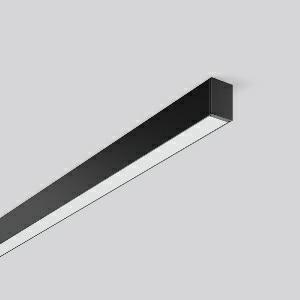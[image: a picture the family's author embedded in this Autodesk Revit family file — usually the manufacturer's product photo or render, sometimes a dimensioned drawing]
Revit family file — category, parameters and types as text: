
# Revit family: less_is_more_27_312200_003_76_f4a9
name_source: partatom
category: Lighting Fixtures
units: mm (PartAtom-declared; Revit-internal decimal feet)

## family parameters
Cut with Voids When Loaded = No
Host = Face
Light Source = No
Part Type = Normal
Room Calculation Point = No
Round Connector Dimension = Use Diameter
Shared = No

## types (1)
- LESS IS MORE 27 (1 x LED Modul 830, 2400 lm, 3000)
    Apparent Load = 43 VA
    CIE Flux Codes = 48 79 96 100 100
    Color Rendering = 80
    Color Temperature = 3000
    Default Elevation = 1800 mm
    Description = Series: LESS IS MORE 27
Ceiling and wall luminaire with slim design. Housing: extruded aluminium profile, powder-coated. End cap aluminium powder-coated. Diffuser made of non-yellowing plastic (PMMA), opal. Suitable for Ceiling mounting, Wall (surface). External driver with connecting cable. 
Colour: deep black, matt (RAL 9005)
Length: 1512 mm
Width: 28 mm
Height: 38 mm
Lamp: LED
Socket: without socket
Colour temperature: 3000K
Colour rendering index (CRI): 82
System power: 43 W
Rated luminous flux: 2400 lm
Luminous efficiency: 56 lm/W
Control gear: Voltage converter, DALI dim.
Protection class: II
Type of protection: IP 20
    Height = 38 mm
    Lamp = 1 x LED Modul 830
    Lamp Light Flux = 2400 lm
    Lamp count = 1
    Length = 1512 mm
    Lifetime = 50000 h
    Luminous efficacy = 56 lm/W
    Manufacturer = RZB
    ModVariant = No
    Model = 312200.003.76
    Mounting Place = Ceiling, Wall
    Mounting Type = Surface mounted
    Number of Poles = 1
    OnlyDefault = Yes
    Power Factor = 1
    Product Name = LESS IS MORE 27
    Product group = Surface mounted LED linear luminaires
    ProductGroupID = 307
    Protection Class = Protection class II
    Protection Degree = IP 20
    RLX_Detail_Level = 1
    RLX_Emergency_Light_Flux = 0 lm
    RLX_Emergency_Type = 0
    RLX_Emergency_Type_DB = No
    RlxData = <blob elided: 28741 chars, md5=8c4a918a>
    Socket = socket
    Standby Power = 0 W
    System Light Flux = 2400 lm
    System Power = 43 W
    Type Comments = Product without accessories
    Type Image = 312196.003.jpg
    URL = http://relux.com
    VarID = ---
    Voltage = 230 V
    Voltage Range = 220-240 V
    Weight = 0.00 kg
    Width = 28 mm

## geometry (parser evidence)
native form markers: Blend x4, Sweep x11
no freeform markers — native parametric forms only
